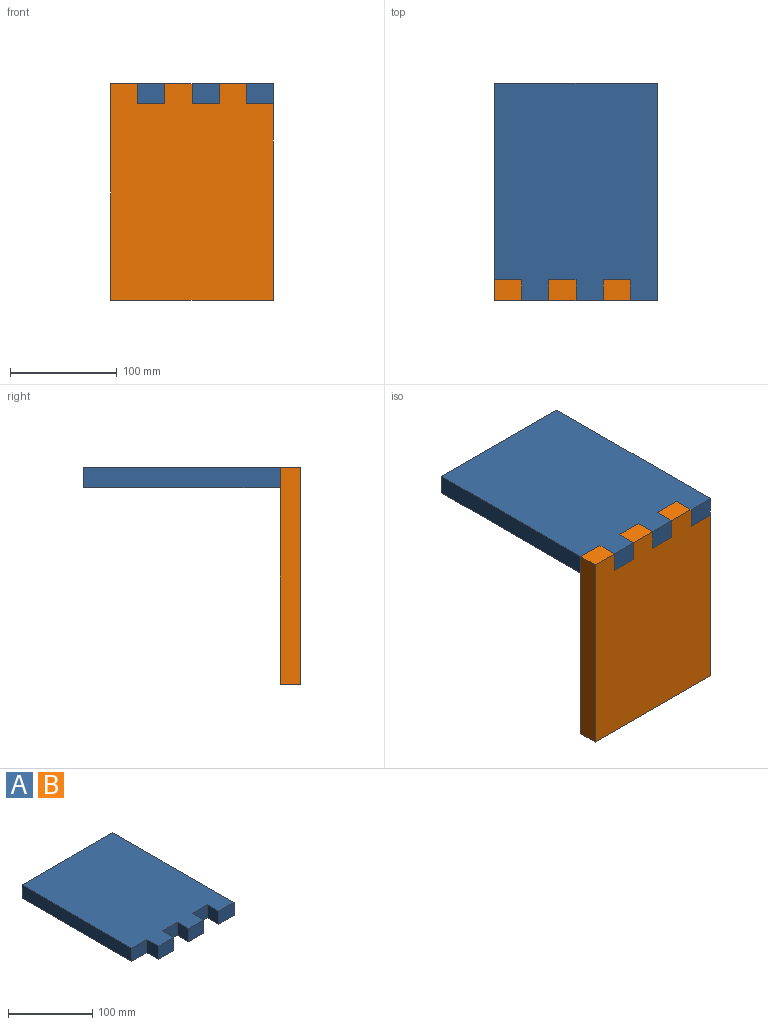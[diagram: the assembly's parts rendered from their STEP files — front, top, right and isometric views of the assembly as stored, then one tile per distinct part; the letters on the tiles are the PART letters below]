
ASSEMBLY  parts=2 mates=1
PART A: 16 faces, bbox 152.4x203.2x19.1 mm
  f0: plane 184.15x19.05mm, normal (-1,0,0), area 3508.1mm2, adj f1,f13,f14,f15
  f1: plane 25.4x19.05mm, normal (0,-1,0), area 483.9mm2, adj f0,f2,f14,f15
  f2: plane 19.05x19.05mm, normal (-1,0,0), area 362.9mm2, adj f1,f3,f14,f15
  f3: plane 25.4x19.05mm, normal (0,-1,0), area 483.9mm2, adj f2,f4,f14,f15
  f4: plane 19.05x19.05mm, normal (1,0,0), area 362.9mm2, adj f3,f5,f14,f15
  f5: plane 25.4x19.05mm, normal (0,-1,0), area 483.9mm2, adj f4,f6,f14,f15
  f6: plane 19.05x19.05mm, normal (-1,0,0), area 362.9mm2, adj f5,f7,f14,f15
  f7: plane 25.4x19.05mm, normal (0,-1,0), area 483.9mm2, adj f6,f8,f14,f15
  f8: plane 19.05x19.05mm, normal (1,0,0), area 362.9mm2, adj f7,f9,f14,f15
  f9: plane 25.4x19.05mm, normal (0,-1,0), area 483.9mm2, adj f8,f10,f14,f15
  f10: plane 19.05x19.05mm, normal (-1,0,0), area 362.9mm2, adj f9,f11,f14,f15
  f11: plane 25.4x19.05mm, normal (0,-1,0), area 483.9mm2, adj f10,f12,f14,f15
  f12: plane 203.2x19.05mm, normal (1,0,0), area 3871mm2, adj f11,f13,f14,f15
  f13: plane 152.4x19.05mm, normal (0,1,0), area 2903.2mm2, adj f0,f12,f14,f15
  f14: plane 203.2x152.4mm, normal (0,0,1), area 29516.1mm2, adj f0,f1,f2,f3,f4,f5,f6,f7
  f15: plane 203.2x152.4mm, normal (0,0,-1), area 29516.1mm2, adj f0,f1,f2,f3,f4,f5,f6,f7
PART B: same geometry as A
PLACE A rot(axis=(0.96,0,0.26),0deg) t=(-114.2,-77.59,41.84)mm
PLACE B rot(axis=(0,-0.71,0.71),180deg) t=(38.2,-58.54,60.89)mm
MATE fastened B.f14 <-> A.f3  axis (0,-1,0) through (-76.1,-77.59,41.84)mm
